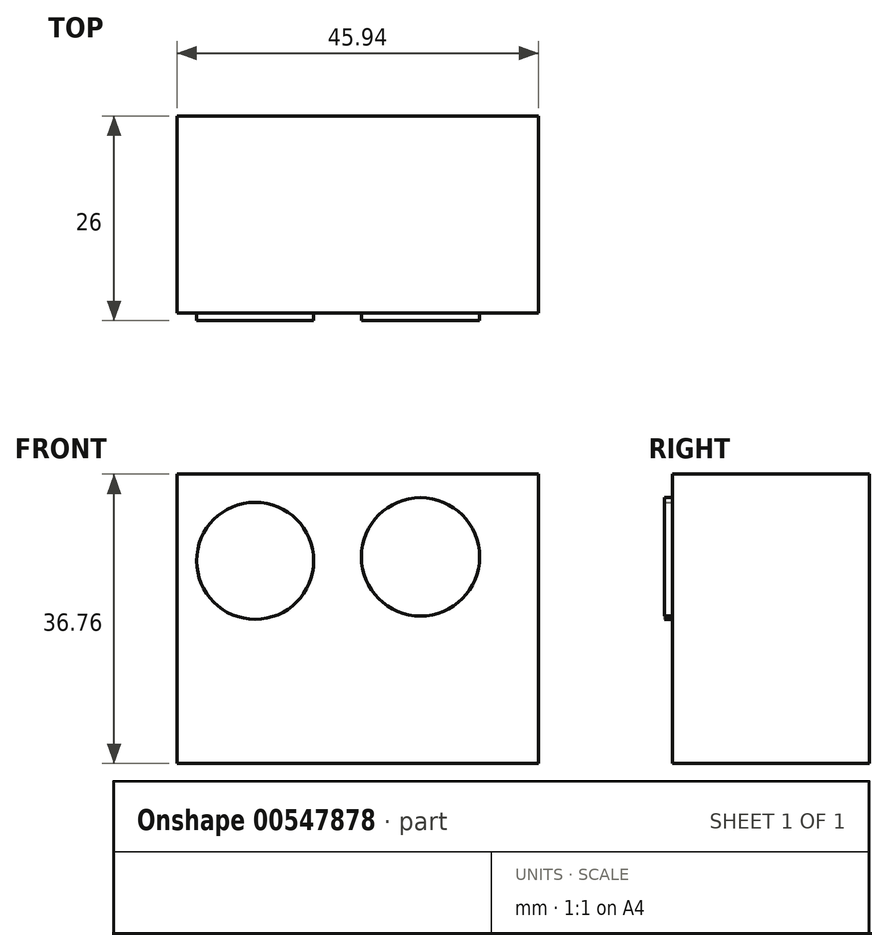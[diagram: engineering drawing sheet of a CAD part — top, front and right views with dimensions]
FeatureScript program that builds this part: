
annotation { "Feature Type Name" : "Feature", "Feature Type Description" : "" }
export const myFeature = defineFeature(function(context is Context, id is Id, definition is map)
    precondition{}
    {
        {
            var Q0;
            Q0=qCreatedBy(makeId("Front.planeOp"),FACE);
            var sketch = newSketch(context, id + "F0", { "sketchPlane" : qUnion([Q0])});
            skLineSegment(sketch, "E0.bottom", {"start": v(-55.36, 41.81) * mm, "end": v(-9.42, 41.81) * mm});
            skLineSegment(sketch, "E0.top", {"start": v(-55.36, 5.05) * mm, "end": v(-9.42, 5.05) * mm});
            skLineSegment(sketch, "E0.left", {"start": v(-55.36, 41.81) * mm, "end": v(-55.36, 5.05) * mm});
            skLineSegment(sketch, "E0.right", {"start": v(-9.42, 41.81) * mm, "end": v(-9.42, 5.05) * mm});
            skSolve(sketch);
        }
        {
            var Q0;
            Q0=makeQuery(id+"F0.imprint","IMPRINT",FACE,{"disambiguationData":[TD([[makeQuery(id+"F0.imprint","IMPRINT",EDGE,{"derivedFrom":sQuery(id+"F0.wireOp",EDGE,"E0.bottom")}),-1.0]])]});
            extrude(context, id + "F1", {"entities" : qUnion([Q0]), "depth" : 25 * mm, "offsetDistance" : 25 * mm});
        }
        {
            var Q0;
            Q0=makeQuery(id+"F1.opExtrude","CAP_FACE",FACE,{"disambiguationData":[OSD([sQuery(id+"F0.wireOp",EDGE,"E0.bottom"),sQuery(id+"F0.wireOp",EDGE,"E0.top"),sQuery(id+"F0.wireOp",EDGE,"E0.left"),sQuery(id+"F0.wireOp",EDGE,"E0.right")])],"isStart":false});
            var sketch = newSketch(context, id + "F2", { "sketchPlane" : qUnion([Q0])});
            skCircle(sketch, "E1", {"center": v(-45.42, 30.8) * mm, "radius": 7.43 * mm});
            skCircle(sketch, "E2", {"center": v(-24.42, 31.3) * mm, "radius": 7.52 * mm});
            skSolve(sketch);
        }
        {
            var Q0;
            Q0 = qSketchRegion(id + "F2", true);
            extrude(context, id + "F3", {"entities" : qUnion([Q0]), "operationType" : NewBodyOperationType.ADD, "depth" : 1 * mm, "offsetDistance" : 25 * mm});
        }
    });
